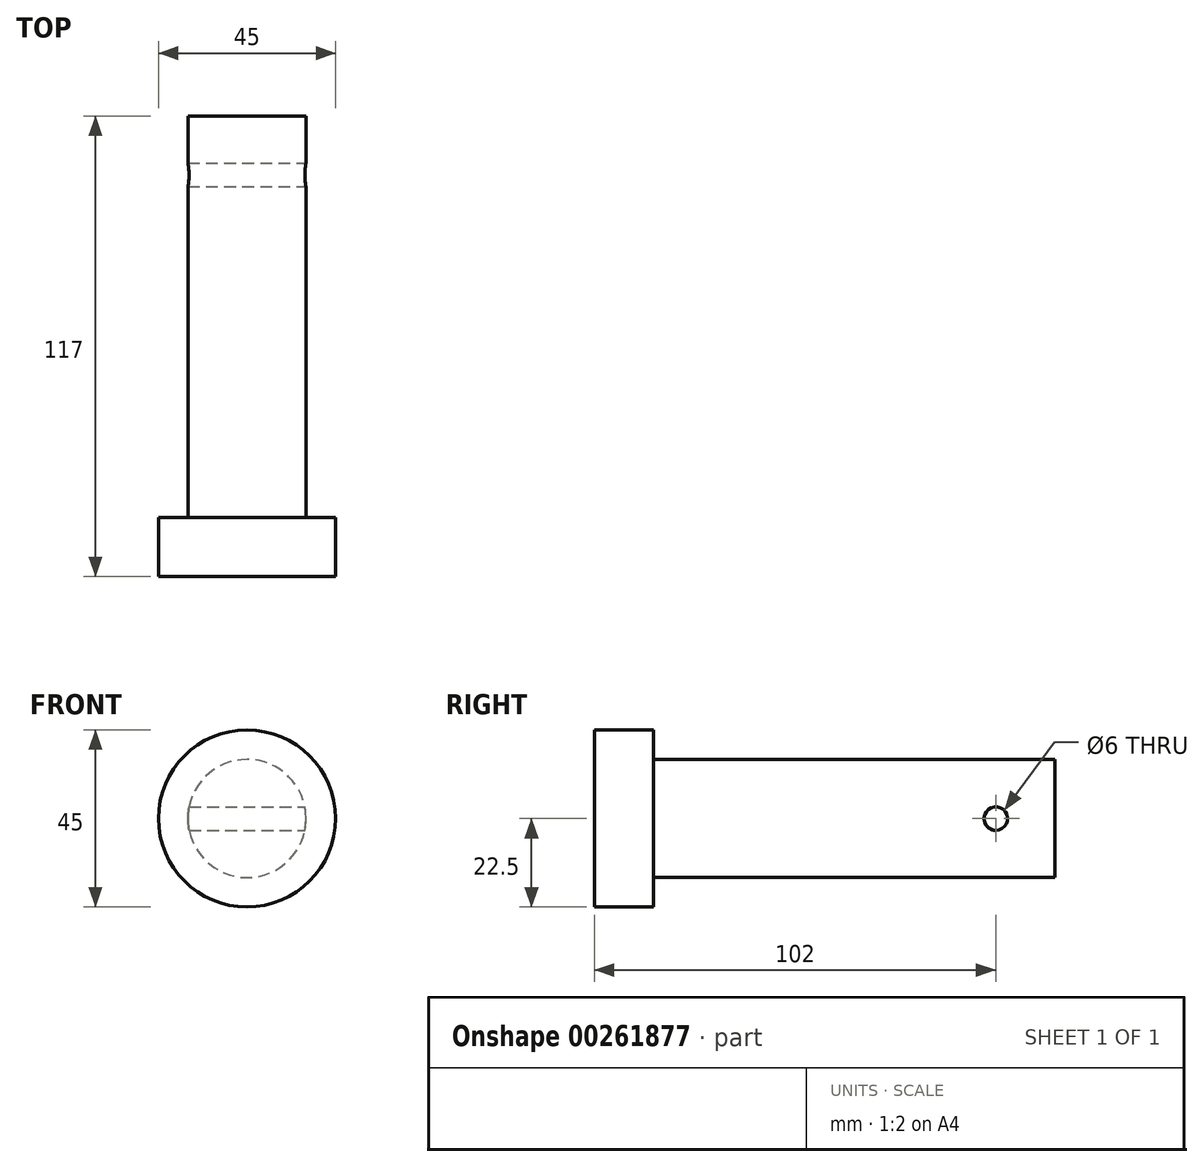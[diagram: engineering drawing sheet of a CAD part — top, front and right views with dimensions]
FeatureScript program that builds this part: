
annotation { "Feature Type Name" : "Feature", "Feature Type Description" : "" }
export const myFeature = defineFeature(function(context is Context, id is Id, definition is map)
    precondition{}
    {
        {
            var Q0;
            Q0=qCreatedBy(makeId("Front.planeOp"),FACE);
            var sketch = newSketch(context, id + "F0", { "sketchPlane" : qUnion([Q0])});
            skCircle(sketch, "E0", {"center": v(0, 0) * mm, "radius": 15 * mm});
            skSolve(sketch);
        }
        {
            var Q0;
            Q0 = qSketchRegion(id + "F0", true);
            extrude(context, id + "F1", {"entities" : qUnion([Q0]), "endBound" : BoundingType.SYMMETRIC, "depth" : 102 * mm});
        }
        {
            var Q0;
            Q0=makeQuery(id+"F1.opExtrude","CAP_FACE",FACE,{"disambiguationData":[OSD([sQuery(id+"F0.wireOp",EDGE,"E0")])],"isStart":false});
            var sketch = newSketch(context, id + "F2", { "sketchPlane" : qUnion([Q0])});
            skCircle(sketch, "E1", {"center": v(0, 0) * mm, "radius": 22.5 * mm});
            skSolve(sketch);
        }
        {
            var Q0;
            Q0 = qSketchRegion(id + "F2", true);
            extrude(context, id + "F3", {"entities" : qUnion([Q0]), "operationType" : NewBodyOperationType.ADD, "depth" : 15 * mm});
        }
        {
            var Q0;
            Q0=qCreatedBy(makeId("Right.planeOp"),FACE);
            var sketch = newSketch(context, id + "F4", { "sketchPlane" : qUnion([Q0])});
            skCircle(sketch, "E2", {"center": v(36, 0) * mm, "radius": 3 * mm});
            skSolve(sketch);
        }
        {
            var Q0;
            Q0 = qSketchRegion(id + "F4", true);
            extrude(context, id + "F5", {"entities" : qUnion([Q0]), "operationType" : NewBodyOperationType.REMOVE, "endBound" : BoundingType.SYMMETRIC, "oppositeDirection" : true, "depth" : 30 * mm});
        }
    });
